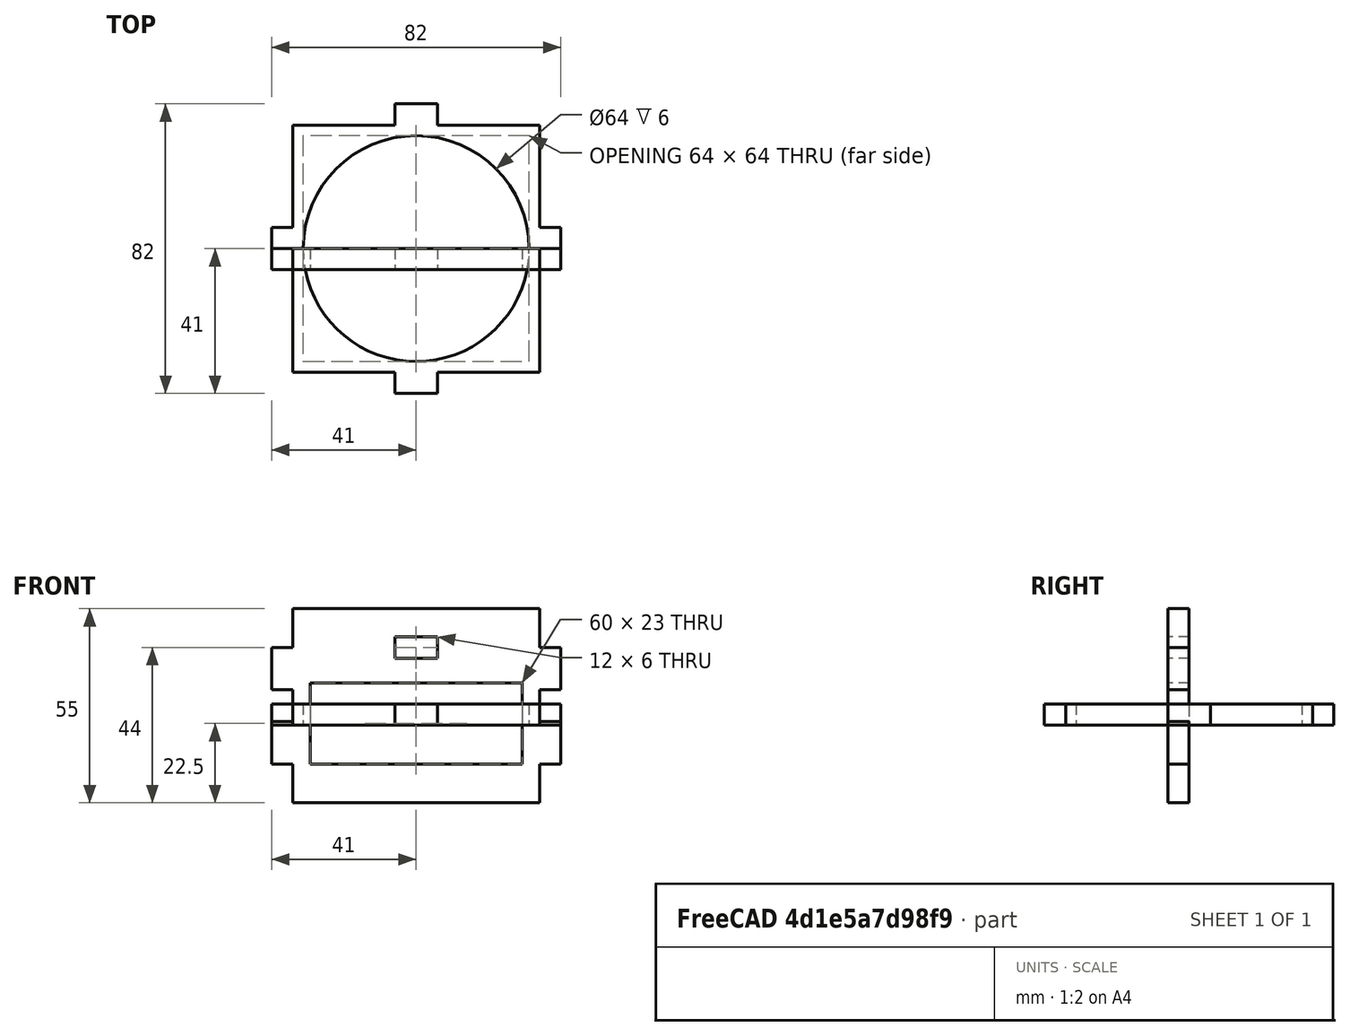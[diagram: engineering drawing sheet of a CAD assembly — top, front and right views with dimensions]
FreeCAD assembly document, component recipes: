
FREECAD ASSEMBLY — COMPONENT RECIPES ("cupholder")

This assembly document has 5 components, labeled P0..P4 below (a component is one placed body or linked part). 5 of them carry a construction recipe — the FreeCAD feature program that regenerates the part from scratch, quoted from this document or its linked companion documents; the rest are supplied as boundary geometry only. No exploded tour is included for this assembly.
COMPONENT P0 — recipe-attached ("cup_place001", modeled in this document).
Construction recipe (the document's own serialized feature program — sketch geometry with constraints, then the solid features built on it; lengths are millimeters unless a unit is written):

FEATURE [Sketcher::SketchObject] Sketch002
  ArcFitTolerance = 1e-06
  AttachmentSupport = -> [XY_Plane004]
  FullyConstrained = true
  MakeInternals = false
  MapMode = 5
  expr: Constraints[21] = VarSet.material
  sketch-geometry (9):
    g0: ArcOfCircle CenterX=0 CenterY=0 CenterZ=0 NormalX=0 NormalY=0 NormalZ=1 AngleXU=0 Radius=32 StartAngle=0 EndAngle=1.5708
    g1: LineSegment StartX=0 StartY=32 StartZ=0 EndX=0 EndY=41 EndZ=0
    g2: LineSegment StartX=0 StartY=41 StartZ=0 EndX=6 EndY=41 EndZ=0
    g3: LineSegment StartX=6 StartY=41 StartZ=0 EndX=6 EndY=35 EndZ=0
    g4: LineSegment StartX=6 StartY=35 StartZ=0 EndX=35 EndY=35 EndZ=0
    g5: LineSegment StartX=35 StartY=35 StartZ=0 EndX=35 EndY=6 EndZ=0
    g6: LineSegment StartX=35 StartY=6 StartZ=0 EndX=41 EndY=6 EndZ=0
    g7: LineSegment StartX=41 StartY=6 StartZ=0 EndX=41 EndY=0 EndZ=0
    g8: LineSegment StartX=41 StartY=0 StartZ=0 EndX=32 EndY=0 EndZ=0
  constraints (27):
    c: Coincident(g0,g-1)
    c: PointOnObject(g0,g-2)
    c: PointOnObject(g0,g-1)
    c: Coincident(g0,g1)
    c: PointOnObject(g1,g-2)
    c: Coincident(g1,g2)
    c: Horizontal(g2)
    c: Coincident(g2,g3)
    c: Vertical(g3)
    c: Coincident(g3,g4)
    c: Horizontal(g4)
    c: Coincident(g4,g5)
    c: Vertical(g5)
    c: Coincident(g5,g6)
    c: Horizontal(g6)
    c: Coincident(g6,g7)
    c: PointOnObject(g7,g-1)
    c: Vertical(g7)
    c: Coincident(g7,g8)
    c: Coincident(g8,g0)
    c: DistanceX(g2,g2) = 6
    c: DistanceY(g3,g3) = 6
    c: Equal(g1,g8)
    c: Equal(g2,g7)
    c: Radius(g0) = 32
    c: Distance(g1,g5) = 35
    c: Distance(g-1,g4) = 35
FEATURE [PartDesign::Pad] Pad002
  Direction = (0,0,1)
  Length = 6
  Length2 = 10
  Profile = -> Sketch002
  ReferenceAxis = -> Sketch002 [N_Axis]
  Refine = true
  Suppressed = false
  Type = 0
  expr: Length = VarSet.material
FEATURE [PartDesign::Mirrored] Mirrored002
  BaseFeature = -> Pad002
  MirrorPlane = -> Sketch002 [V_Axis]
  Originals = -> [Pad002]
  Refine = true
  Suppressed = false
  TransformMode = 0
FEATURE [PartDesign::Mirrored] Mirrored003
  BaseFeature = -> Mirrored002
  MirrorPlane = -> XZ_Plane004
  Originals = -> [Mirrored002]
  Refine = true
  Suppressed = false
  TransformMode = 1
FEATURE [PartDesign::Body] Body003  label="cup_place"
  AllowCompound = false
  Group = -> [Sketch002,Pad002,Mirrored002,Mirrored003]
  Origin = -> Origin004
  Tip = -> Mirrored003
COMPONENT P1 — recipe-attached ("in_part001", modeled in this document).
Construction recipe (the document's own serialized feature program — sketch geometry with constraints, then the solid features built on it; lengths are millimeters unless a unit is written):

FEATURE [Sketcher::SketchObject] Sketch001
  ArcFitTolerance = 1e-06
  AttachmentSupport = -> [XZ_Plane002]
  FullyConstrained = true
  MakeInternals = false
  MapMode = 5
  Placement = pos=(0,0,0) rot=(1,0,0;1.5708rad)
  expr: Constraints[22] = 35 mm + VarSet.material
  expr: Constraints[26] = VarSet.material
  expr: Constraints[52] = VarSet.material
  sketch-geometry (20):
    g0: LineSegment StartX=0 StartY=33 StartZ=0 EndX=41 EndY=33 EndZ=0
    g1: LineSegment StartX=41 StartY=33 StartZ=0 EndX=41 EndY=22 EndZ=0
    g2: LineSegment StartX=41 StartY=22 StartZ=0 EndX=35 EndY=22 EndZ=0
    g3: LineSegment StartX=35 StartY=22 StartZ=0 EndX=35 EndY=10 EndZ=0
    g4: LineSegment StartX=35 StartY=10 StartZ=0 EndX=41 EndY=10 EndZ=0
    g5: LineSegment StartX=41 StartY=10 StartZ=0 EndX=41 EndY=1 EndZ=0
    g6: LineSegment StartX=41 StartY=1 StartZ=0 EndX=35 EndY=1 EndZ=0
    g7: LineSegment StartX=35 StartY=1 StartZ=0 EndX=35 EndY=-11 EndZ=0
    g8: LineSegment StartX=35 StartY=-11 StartZ=0 EndX=41 EndY=-11 EndZ=0
    g9: LineSegment StartX=41 StartY=-11 StartZ=0 EndX=41 EndY=-22 EndZ=0
    g10: LineSegment StartX=41 StartY=-22 StartZ=0 EndX=0 EndY=-22 EndZ=0
    g11: LineSegment StartX=0 StartY=33 StartZ=0 EndX=0 EndY=25 EndZ=0
    g12: LineSegment StartX=0 StartY=25 StartZ=0 EndX=6 EndY=25 EndZ=0
    g13: LineSegment StartX=6 StartY=25 StartZ=0 EndX=6 EndY=19 EndZ=0
    g14: LineSegment StartX=6 StartY=19 StartZ=0 EndX=0 EndY=19 EndZ=0
    g15: LineSegment StartX=0 StartY=19 StartZ=0 EndX=0 EndY=12 EndZ=0
    g16: LineSegment StartX=0 StartY=12 StartZ=0 EndX=30 EndY=12 EndZ=0
    g17: LineSegment StartX=30 StartY=12 StartZ=0 EndX=30 EndY=-11 EndZ=0
    g18: LineSegment StartX=30 StartY=-11 StartZ=0 EndX=0 EndY=-11 EndZ=0
    g19: LineSegment StartX=0 StartY=-11 StartZ=0 EndX=0 EndY=-22 EndZ=0
  constraints (60):
    c: PointOnObject(g0,g-2)
    c: Horizontal(g0)
    c: Coincident(g0,g1)
    c: Vertical(g1)
    c: Coincident(g1,g2)
    c: Horizontal(g2)
    c: Coincident(g2,g3)
    c: Vertical(g3)
    c: Coincident(g3,g4)
    c: Horizontal(g4)
    c: Coincident(g4,g5)
    c: Vertical(g5)
    c: Coincident(g5,g6)
    c: Horizontal(g6)
    c: Coincident(g6,g7)
    c: Vertical(g7)
    c: Coincident(g7,g8)
    c: Horizontal(g8)
    c: Coincident(g8,g9)
    c: Vertical(g9)
    c: Coincident(g9,g10)
    c: PointOnObject(g10,g-2)
    c: DistanceX(g0,g0) = 41
    c: Equal(g0,g10)
    c: Horizontal(g10)
    c: DistanceY(g3,g3) = 12
    c: DistanceX(g4,g4) = 6
    c: Equal(g2,g4)
    c: Equal(g4,g6)
    c: Equal(g3,g7)
    c: Distance(g10,g0) = 55
    c: DistanceY(g9,g9) = 11
    c: Distance(g-1,g10) = 22
    c: Equal(g1,g9)
    c: Coincident(g0,g11)
    c: PointOnObject(g11,g-2)
    c: Coincident(g11,g12)
    c: Horizontal(g12)
    c: Coincident(g12,g13)
    c: Coincident(g13,g14)
    c: PointOnObject(g14,g-2)
    c: Horizontal(g14)
    c: Coincident(g14,g15)
    c: PointOnObject(g15,g-2)
    c: Coincident(g15,g16)
    c: Horizontal(g16)
    c: Coincident(g16,g17)
    c: Vertical(g17)
    c: Coincident(g17,g18)
    c: PointOnObject(g18,g-2)
    c: Coincident(g18,g19)
    c: Coincident(g19,g10)
    c: DistanceY(g13,g13) = 6
    c: DistanceY(g11,g11) = 8
    c: DistanceX(g12,g12) = 6
    c: Vertical(g13)
    c: DistanceY(g15,g15) = 7
    c: DistanceY(g19,g19) = 11
    c: Horizontal(g18)
    c: DistanceX(g18,g18) = 30
FEATURE [PartDesign::Pad] Pad001
  Direction = (0,-1,2e-16)
  Length = 6
  Length2 = 10
  Placement = pos=(0,0,0) rot=(1,0,0;1.5708rad)
  Profile = -> Sketch001
  ReferenceAxis = -> Sketch001 [N_Axis]
  Refine = true
  Suppressed = false
  Type = 0
  expr: Length = VarSet.material
FEATURE [PartDesign::Mirrored] Mirrored001
  BaseFeature = -> Pad001
  MirrorPlane = -> Sketch001 [V_Axis]
  Originals = -> [Pad001]
  Placement = pos=(0,0,0) rot=(1,0,0;1.5708rad)
  Refine = true
  Suppressed = false
  TransformMode = 0
FEATURE [PartDesign::Body] Body002  label="in_part"
  AllowCompound = false
  Group = -> [Sketch001,Pad001,Mirrored001]
  Origin = -> Origin002
  Tip = -> Mirrored001
COMPONENT P2 — same part as P1; its construction recipe is shown at P1.
COMPONENT P3 — recipe-attached ("out_part001", modeled in this document).
Construction recipe (the document's own serialized feature program — sketch geometry with constraints, then the solid features built on it; lengths are millimeters unless a unit is written):

FEATURE [Sketcher::SketchObject] Sketch
  ArcFitTolerance = 1e-06
  AttachmentSupport = -> [XZ_Plane]
  FullyConstrained = true
  MakeInternals = false
  MapMode = 5
  Placement = pos=(0,0,0) rot=(1,0,0;1.5708rad)
  expr: Constraints[24] = VarSet.material
  expr: Constraints[55] = VarSet.material
  sketch-geometry (20):
    g0: LineSegment StartX=0 StartY=33 StartZ=0 EndX=35 EndY=33 EndZ=0
    g1: LineSegment StartX=35 StartY=33 StartZ=0 EndX=35 EndY=22 EndZ=0
    g2: LineSegment StartX=35 StartY=22 StartZ=0 EndX=41 EndY=22 EndZ=0
    g3: LineSegment StartX=41 StartY=22 StartZ=0 EndX=41 EndY=10 EndZ=0
    g4: LineSegment StartX=41 StartY=10 StartZ=0 EndX=35 EndY=10 EndZ=0
    g5: LineSegment StartX=35 StartY=10 StartZ=0 EndX=35 EndY=1 EndZ=0
    g6: LineSegment StartX=35 StartY=1 StartZ=0 EndX=41 EndY=1 EndZ=0
    g7: LineSegment StartX=41 StartY=1 StartZ=0 EndX=41 EndY=-11 EndZ=0
    g8: LineSegment StartX=41 StartY=-11 StartZ=0 EndX=35 EndY=-11 EndZ=0
    g9: LineSegment StartX=35 StartY=-11 StartZ=0 EndX=35 EndY=-22 EndZ=0
    g10: LineSegment StartX=35 StartY=-22 StartZ=0 EndX=0 EndY=-22 EndZ=0
    g11: LineSegment StartX=0 StartY=33 StartZ=0 EndX=0 EndY=25 EndZ=0
    g12: LineSegment StartX=0 StartY=25 StartZ=0 EndX=6 EndY=25 EndZ=0
    g13: LineSegment StartX=6 StartY=25 StartZ=0 EndX=6 EndY=19 EndZ=0
    g14: LineSegment StartX=6 StartY=19 StartZ=0 EndX=0 EndY=19 EndZ=0
    g15: LineSegment StartX=0 StartY=19 StartZ=0 EndX=0 EndY=12 EndZ=0
    g16: LineSegment StartX=0 StartY=12 StartZ=0 EndX=30 EndY=12 EndZ=0
    g17: LineSegment StartX=30 StartY=12 StartZ=0 EndX=30 EndY=-11 EndZ=0
    g18: LineSegment StartX=30 StartY=-11 StartZ=0 EndX=0 EndY=-11 EndZ=0
    g19: LineSegment StartX=0 StartY=-11 StartZ=0 EndX=0 EndY=-22 EndZ=0
  constraints (60):
    c: PointOnObject(g0,g-2)
    c: Horizontal(g0)
    c: Coincident(g0,g1)
    c: Vertical(g1)
    c: Coincident(g1,g2)
    c: Horizontal(g2)
    c: Coincident(g2,g3)
    c: Vertical(g3)
    c: Coincident(g3,g4)
    c: Coincident(g4,g5)
    c: Vertical(g5)
    c: Coincident(g5,g6)
    c: Horizontal(g6)
    c: Coincident(g6,g7)
    c: Vertical(g7)
    c: Coincident(g7,g8)
    c: Coincident(g8,g9)
    c: Coincident(g9,g10)
    c: PointOnObject(g10,g-2)
    c: Horizontal(g10)
    c: Horizontal(g8)
    c: Horizontal(g4)
    c: Vertical(g9)
    c: Distance(g10,g0) = 55
    c: DistanceX(g2,g2) = 6
    c: Equal(g2,g4)
    c: Equal(g4,g6)
    c: Equal(g6,g8)
    c: DistanceY(g3,g3) = 12
    c: Equal(g3,g7)
    c: DistanceX(g0,g0) = 35
    c: DistanceY(g9,g9) = 11
    c: Distance(g10,g-1) = 22
    c: Equal(g1,g9)
    c: Coincident(g0,g11)
    c: Vertical(g11)
    c: Coincident(g11,g12)
    c: Horizontal(g12)
    c: Coincident(g12,g13)
    c: Vertical(g13)
    c: Coincident(g13,g14)
    c: PointOnObject(g14,g-2)
    c: Horizontal(g14)
    c: Coincident(g14,g15)
    c: PointOnObject(g15,g-2)
    c: Coincident(g15,g16)
    c: Horizontal(g16)
    c: Coincident(g16,g17)
    c: Vertical(g17)
    c: Coincident(g17,g18)
    c: PointOnObject(g18,g-2)
    c: Horizontal(g18)
    c: Coincident(g18,g19)
    c: Coincident(g19,g10)
    c: DistanceY(g11,g11) = 8
    c: DistanceY(g13,g13) = 6
    c: Distance(g19,g19) = 11
    c: DistanceX(g18,g18) = 30
    c: DistanceY(g15,g15) = 7
    c: DistanceX(g14,g14) = 6
FEATURE [PartDesign::Pad] Pad
  Direction = (0,-1,2e-16)
  Length = 6
  Length2 = 10
  Placement = pos=(0,0,0) rot=(1,0,0;1.5708rad)
  Profile = -> Sketch
  ReferenceAxis = -> Sketch [N_Axis]
  Refine = true
  Suppressed = false
  Type = 0
  expr: Length = VarSet.material
FEATURE [PartDesign::Mirrored] Mirrored
  BaseFeature = -> Pad
  MirrorPlane = -> Sketch [V_Axis]
  Originals = -> [Pad]
  Placement = pos=(0,0,0) rot=(1,0,0;1.5708rad)
  Refine = true
  Suppressed = false
  TransformMode = 0
FEATURE [PartDesign::Body] Body  label="out_part"
  AllowCompound = false
  Group = -> [Sketch,Pad,Mirrored]
  Origin = -> Origin
  Tip = -> Mirrored
COMPONENT P4 — same part as P3; its construction recipe is shown at P3.
PROVENANCE & LICENSES
A FreeCAD (.FCStd) document from a public repository crawl; recipes are the document's own serialized feature recipes (and, for linked parts, companion documents' recipes).
License: as declared in the source repository (recorded in the dataset sidecar).
